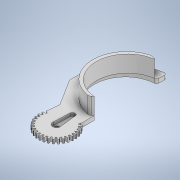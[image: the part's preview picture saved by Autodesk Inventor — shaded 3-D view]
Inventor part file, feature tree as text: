
AUTODESK INVENTOR PART (.ipt)
format: ipt  version: 2021 (Build 250183000, 183)  size: 517,632 bytes
history: native  units: mm
features: extrude x12, sketch x11, fillet x11
ambient origin geometry x8: Origin, YZ Plane, XZ Plane, XY Plane, X Axis, Y Axis, Z Axis, Center Point
bodies: Solid1 (feature_tree)
feature tree (34):
  extrude  "Extrusion1"  Depth=30.0mm
  extrude  "Extrusion4"  Depth=0.5mm
  sketch  "Sketch7"  dims[d13=60.0mm d14=30.0mm d15=10.0mm d19=4.0mm d20=0.0mm]
  extrude  "Extrusion2"  Depth=15.0mm TaperAngle=360.0deg
  fillet  "Fillet13"  Radius=15.0mm
  extrude  "Extrusion14"  Depth=30.0mm
  fillet  "Fillet14"  Radius=10.0mm
  fillet  "Fillet15"  Radius=4.0mm
  extrude  "Extrusion8"  Depth=0.1mm
  extrude  "Extrusion9"  Depth=3.0mm TaperAngle=0.0deg
  fillet  "Fillet4"  Radius=3.0mm
  extrude  "Extrusion10"  Depth=10.0mm TaperAngle=0.0deg
  fillet  "Fillet5"  Radius=40.0mm
  fillet  "Fillet6"  Radius=15.0mm
  fillet  "Fillet7"  Radius=40.0mm
  fillet  "Fillet9"  Radius=40.0mm
  fillet  "Fillet10"  Radius=4.0mm
  extrude  "Extrusion11"  Depth=16.0mm TaperAngle=0.0deg
  fillet  "Fillet11"  Radius=2.0mm
  extrude  "Extrusion12"  Depth=4.0mm
  fillet  "Fillet12"  Radius=21.0mm
  extrude  "Extrusion13"  Depth=2.0mm
  extrude  "Extrusion3"  Depth=4.0mm TaperAngle=0.0deg
  extrude  "Extrusion5"  Depth=3.5mm
  sketch  "Sketch6"  dims[d6=0.1mm d7=310.0mm d9=360.0deg d12=15.0mm]
  sketch  "Sketch4"  dims[d0=30.0mm d1=35.0mm]
  sketch  "Sketch5"  dims[d2=0.5mm d4=0.5mm]
  sketch  "Sketch10"  dims[d22=7.5mm d23=0.1mm]
  sketch  "Sketch11"  dims[d24=2.0mm d25=3.0mm d26=0.0mm d27=3.0mm d28=0.0mm]
  sketch  "Sketch12"  dims[d29=5.0mm d30=10.0mm d31=0.0mm d32=40.0mm d33=15.0mm d34=0.0mm d42=40.0mm d43=40.0mm d44=4.0mm d45=0.0mm]
  sketch  "Sketch13"  dims[d46=40.0mm d47=16.0mm d48=0.0mm d49=2.0mm]
  sketch  "Sketch14"  dims[d50=4.0mm d51=0.0mm d52=234.0mm d53=21.0mm]
  sketch  "Sketch15"  dims[d54=10.0mm d56=2.0mm]
  sketch  "Sketch16"  dims[d57=1.75mm d58=4.0mm d59=0.0mm d60=1.75mm d61=16.0mm d62=0.0mm d63=2.0mm d64=3.0mm d65=0.0mm d66=2.0mm d67=16.0mm d68=0.0mm d69=6.25mm d70=3.5mm d11=0.5mm]
